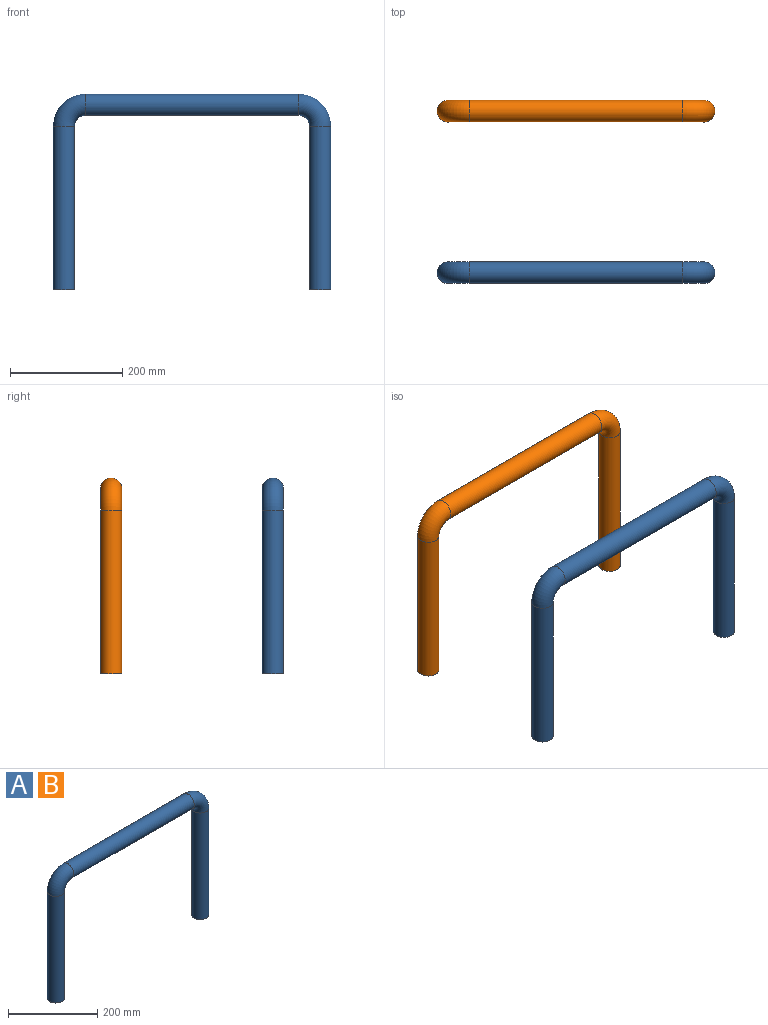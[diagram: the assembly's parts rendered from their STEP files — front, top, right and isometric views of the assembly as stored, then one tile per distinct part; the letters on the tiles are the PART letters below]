
ASSEMBLY  parts=2 mates=2
PART A: 12 faces, bbox 504.7x38.1x354 mm
  f0: cylinder r=15.88mm len=292.1mm, axis (0,0,1), area 29135.7mm2, adj f1,f5
  f1: torus R=38.1mm, axis (0,1,0), area 5969.5mm2, adj f0,f2
  f2: cylinder r=15.88mm len=381mm, axis (1,0,0), area 38003.1mm2, adj f1,f3
  f3: torus R=38.1mm, axis (0,1,0), area 5969.5mm2, adj f2,f4
  f4: cylinder r=15.88mm len=292.1mm, axis (0,0,-1), area 29135.7mm2, adj f3,f6
  f5: plane 38.1x38.1mm, normal (0,0,-1), area 348.4mm2, adj f0,f7
  f6: plane 38.1x38.1mm, normal (0,0,-1), area 348.4mm2, adj f4,f11
  f7: cylinder r=19.05mm len=292.1mm, axis (0,0,1), area 34962.8mm2, adj f5,f8
  f8: torus R=38.1mm, axis (0,1,0), area 7163.4mm2, adj f7,f9
  f9: cylinder r=19.05mm len=381mm, axis (1,0,0), area 45603.7mm2, adj f8,f10
  f10: torus R=38.1mm, axis (0,1,0), area 7163.4mm2, adj f9,f11
  f11: cylinder r=19.05mm len=292.1mm, axis (0,0,-1), area 34962.8mm2, adj f6,f10
PART B: same geometry as A
PLACE A t=(-65.02,64.74,-67.96)mm fixed
PLACE B t=(-65.02,352.9,-67.96)mm
MATE planar B.f9 <-> A.f9  axis (1,0,0) through (163.58,352.9,262.24)mm
MATE planar A.f7 <-> B.f7  axis (0,0,-1) through (-65.02,64.74,-67.96)mm
